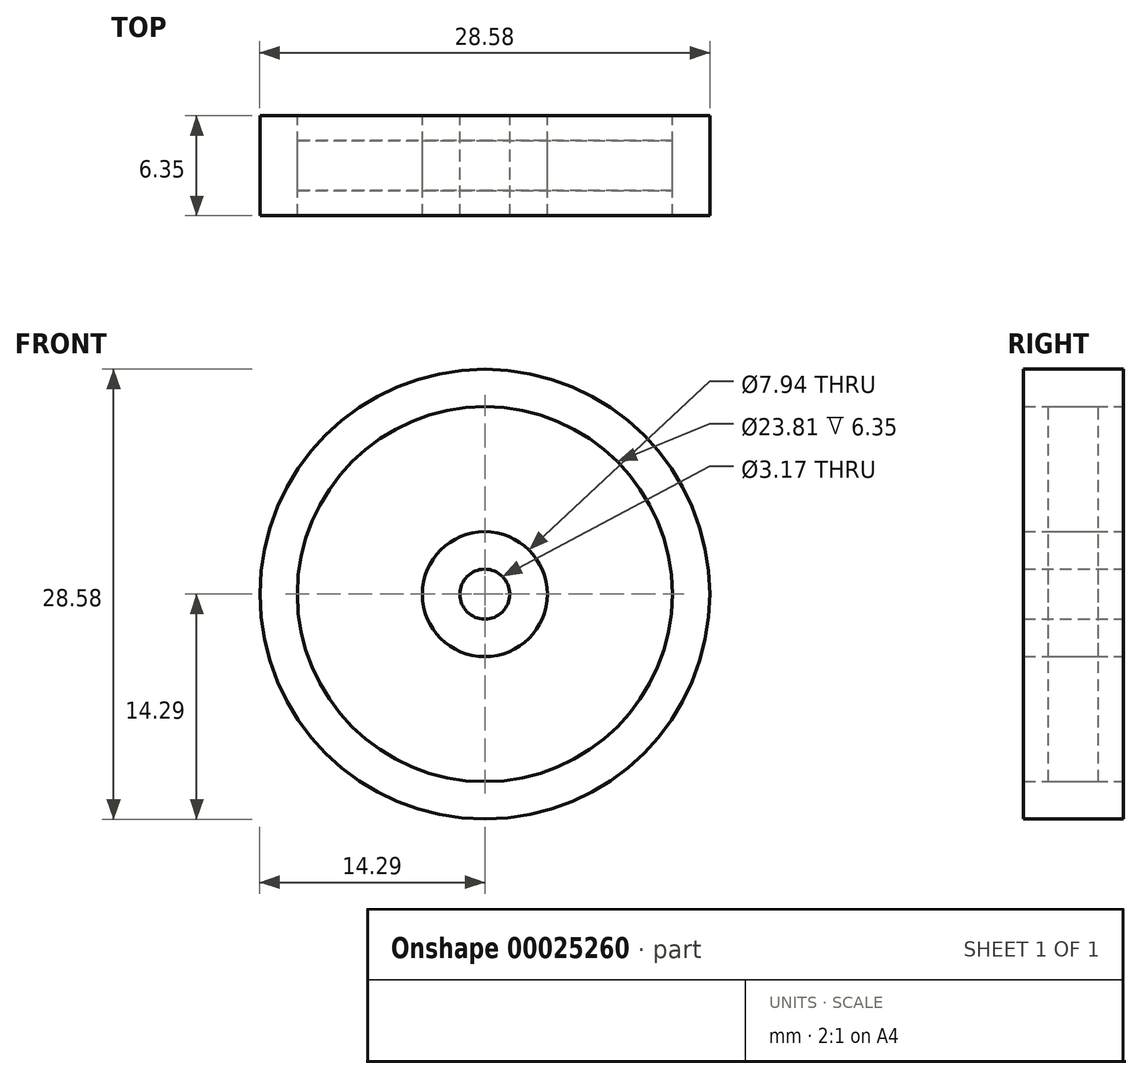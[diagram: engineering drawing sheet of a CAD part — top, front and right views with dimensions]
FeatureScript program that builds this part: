
annotation { "Feature Type Name" : "Feature", "Feature Type Description" : "" }
export const myFeature = defineFeature(function(context is Context, id is Id, definition is map)
    precondition{}
    {
        {
            var Q0;
            Q0=qCreatedBy(makeId("Front.planeOp"),FACE);
            var sketch = newSketch(context, id + "F0", { "sketchPlane" : qUnion([Q0])});
            skCircle(sketch, "E0", {"center": v(0, 0) * mm, "radius": 14.29 * mm});
            skCircle(sketch, "E1", {"center": v(0, 0) * mm, "radius": 11.9 * mm});
            skCircle(sketch, "E2", {"center": v(0, 0) * mm, "radius": 3.97 * mm});
            skCircle(sketch, "E3", {"center": v(0, 0) * mm, "radius": 1.59 * mm});
            skSolve(sketch);
        }
        {
            var Q0;
            Q0=qSketchRegion(id+"F0",true);
            var Q1;
            Q1=makeQuery(id+"F0.imprint","IMPRINT",FACE,{"disambiguationData":[TD([[makeQuery(id+"F0.imprint","IMPRINT",EDGE,{"derivedFrom":sQuery(id+"F0.wireOp",EDGE,"E0")}),1.0]])]});
            var Q2;
            Q2=makeQuery(id+"F0.imprint","IMPRINT",FACE,{"disambiguationData":[TD([[makeQuery(id+"F0.imprint","IMPRINT",EDGE,{"derivedFrom":sQuery(id+"F0.wireOp",EDGE,"E2")}),1.0]])]});
            extrude(context, id + "F1", {"entities" : qUnion([Q0, Q1, Q2]), "depth" : 6.35 * mm});
        }
        {
            var Q0;
            Q0=makeQuery(id+"F0.imprint","IMPRINT",FACE,{"disambiguationData":[TD([[makeQuery(id+"F0.imprint","IMPRINT",EDGE,{"derivedFrom":sQuery(id+"F0.wireOp",EDGE,"E1")}),1.0]])]});
            extrude(context, id + "F2", {"entities" : qUnion([Q0]), "depth" : 4.76 * mm, "hasSecondDirection" : true, "secondDirectionOppositeDirection" : false, "secondDirectionDepth" : 1.59 * mm});
        }
    });
